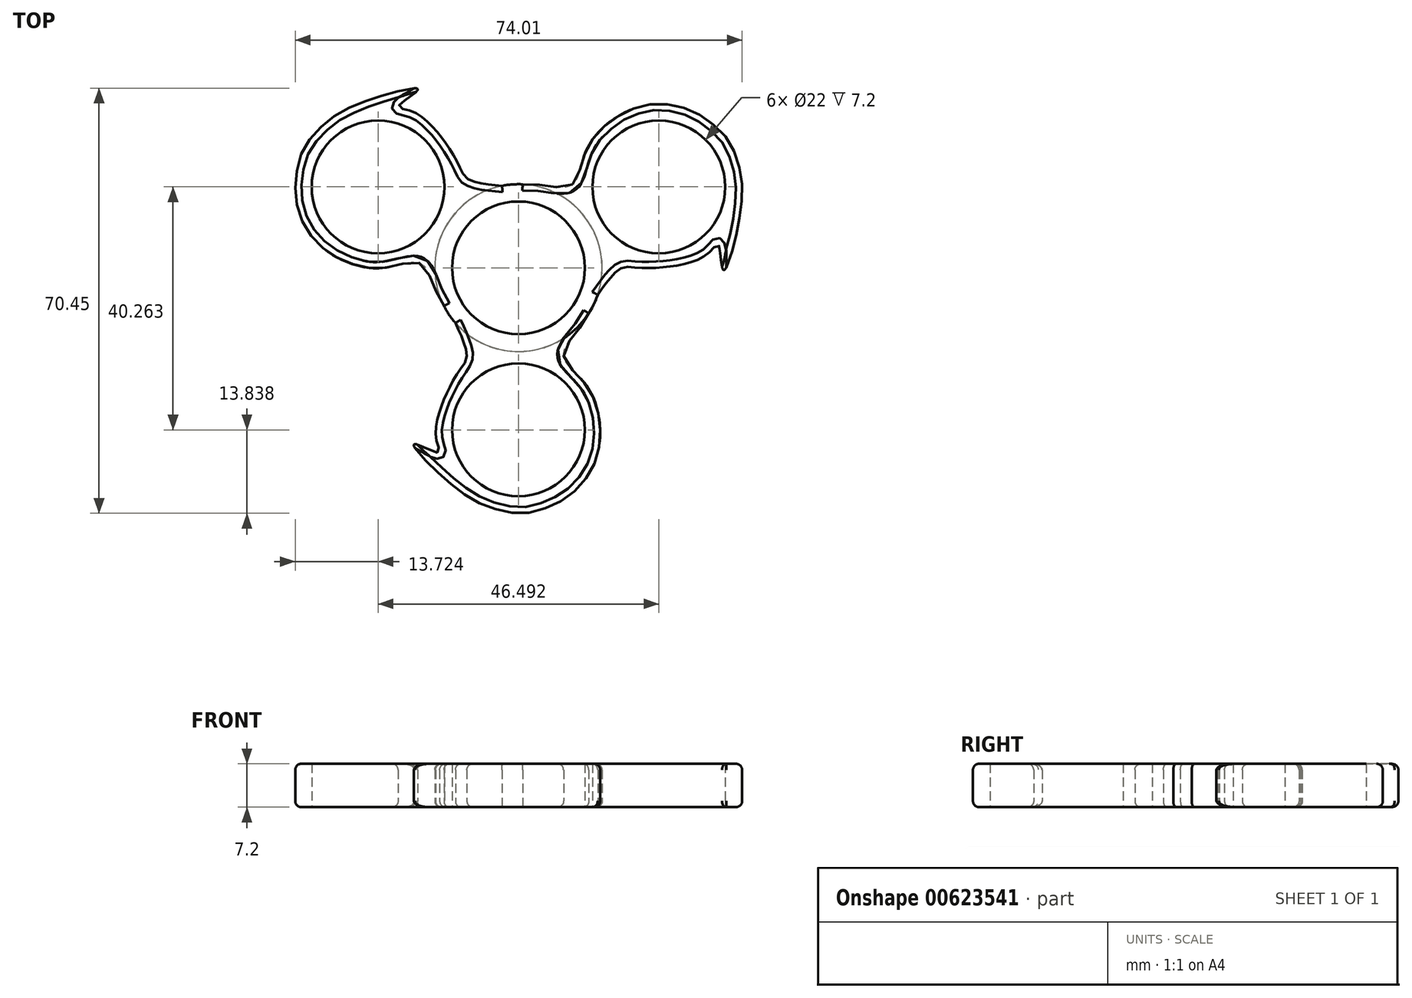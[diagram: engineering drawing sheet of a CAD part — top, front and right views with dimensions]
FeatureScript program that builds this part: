
annotation { "Feature Type Name" : "Feature", "Feature Type Description" : "" }
export const myFeature = defineFeature(function(context is Context, id is Id, definition is map)
    precondition{}
    {
        {
            var Q0;
            Q0=qCreatedBy(makeId("Top.planeOp"),FACE);
            var sketch = newSketch(context, id + "F0", { "sketchPlane" : qUnion([Q0])});
            skCircle(sketch, "E0", {"center": v(0, 0) * mm, "radius": 11 * mm});
            skCircle(sketch, "E1", {"center": v(0, -26.84) * mm, "radius": 11 * mm});
            skCircle(sketch, "E2", {"center": v(0, 0) * mm, "radius": 13.86 * mm});
            skLineSegment(sketch, "E3", {"start": v(0, 0) * mm, "end": v(0, -53.68) * mm, "construction": true});
            skFitSpline(sketch, "E4", {"points": [v(11.65, -7.52) * mm, v(9.7, -10.52) * mm, v(7.48, -14.55) * mm, v(11.48, -19.8) * mm, v(13.37, -29.5) * mm, v(10.69, -35.54) * mm, v(6.87, -38.72) * mm, v(2.5, -40.42) * mm, v(-0.17, -40.67) * mm, v(-3.15, -40.17) * mm, v(-9.64, -37.02) * mm, v(-17.24, -29.21) * mm, v(-13.24, -30.62) * mm, v(-13.7, -27.85) * mm, v(-9.88, -17.15) * mm, v(-8.54, -14.62) * mm, v(-10.42, -9.14) * mm], "startDerivative": vector(-32.29, -56) * mm, "endDerivative": vector(-44.62, 97.98) * mm});
            skSolve(sketch);
        }
        {
            var Q0;
            Q0=qSketchRegion(id+"F0",true);
            extrude(context, id + "F1", {"entities" : qUnion([Q0]), "depth" : 7.2 * mm, "offsetDistance" : 25 * mm});
        }
        {
            var Q0;
            Q0=makeQuery(id+"F1.opExtrude","CAP_EDGE",EDGE,{"disambiguationData":[OSD([sQuery(id+"F0.wireOp",EDGE,"E4")])],"isStart":true});
            var Q1;
            Q1=makeQuery(id+"F1.opExtrude","CAP_EDGE",EDGE,{"disambiguationData":[OSD([sQuery(id+"F0.wireOp",EDGE,"E2")])],"isStart":true});
            var Q2;
            Q2=makeQuery(id+"F1.opExtrude","CAP_EDGE",EDGE,{"disambiguationData":[OSD([sQuery(id+"F0.wireOp",EDGE,"E4")])],"isStart":false});
            var Q3;
            Q3=makeQuery(id+"F1.opExtrude","CAP_EDGE",EDGE,{"disambiguationData":[OSD([sQuery(id+"F0.wireOp",EDGE,"E2")])],"isStart":false});
            fillet(context, id + "F2", {"entities" : qUnion([Q0, Q1, Q2, Q3]), "radius" : 1.02 * mm, "tangentPropagation" : true, "allowEdgeOverflow" : false});
        }
        {
            var Q0;
            Q0=makeQuery(id+"F1.opExtrude","SWEPT_BODY",BODY,{"disambiguationData":[OSD([sQuery(id+"F0.wireOp",EDGE,"E0"),sQuery(id+"F0.wireOp",EDGE,"E1"),sQuery(id+"F0.wireOp",EDGE,"E2"),sQuery(id+"F0.wireOp",EDGE,"E4")])]});
            var Q1;
            Q1=makeQuery(id+"F1.opExtrude","CAP_EDGE",EDGE,{"disambiguationData":[OSD([sQuery(id+"F0.wireOp",EDGE,"E0")])],"isStart":false});
            circularPattern(context, id + "F3", {"entities" : qUnion([Q0]), "axis" : qUnion([Q1]), "angle" : 360 * degree, "instanceCount" : 3, "oppositeDirection" : true, "equalSpace" : true});
        }
    });
